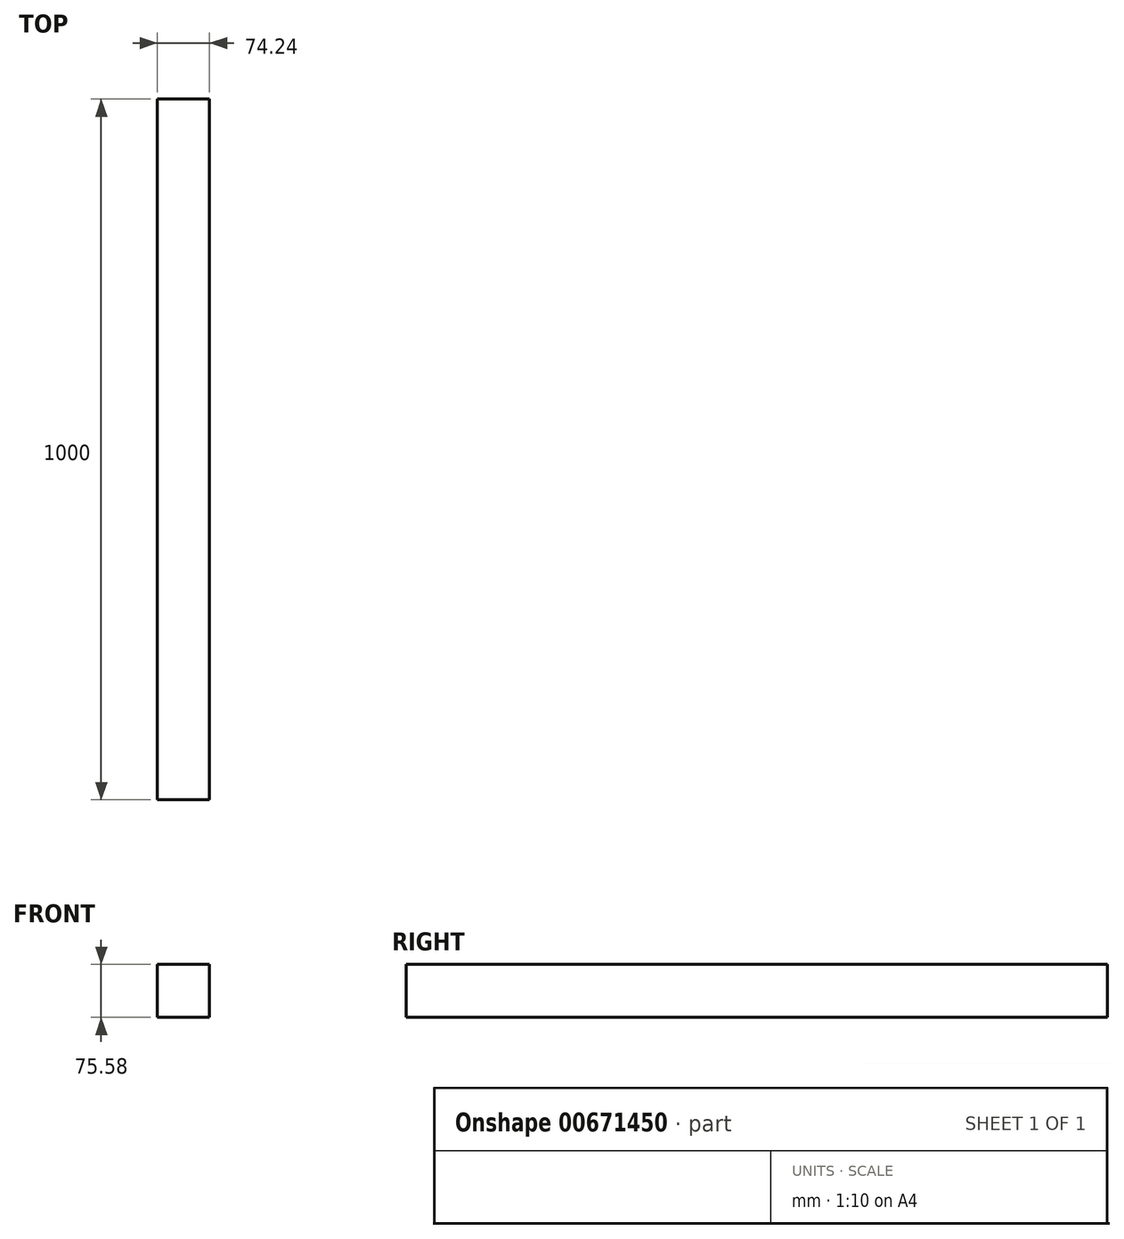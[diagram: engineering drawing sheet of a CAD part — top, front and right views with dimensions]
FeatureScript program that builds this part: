
annotation { "Feature Type Name" : "Feature", "Feature Type Description" : "" }
export const myFeature = defineFeature(function(context is Context, id is Id, definition is map)
    precondition{}
    {
        {
            var Q0;
            Q0=qCreatedBy(makeId("Front.planeOp"),FACE);
            var sketch = newSketch(context, id + "F0", { "sketchPlane" : qUnion([Q0])});
            skLineSegment(sketch, "E0.bottom", {"start": v(-74.24, 0) * mm, "end": v(0, 0) * mm});
            skLineSegment(sketch, "E0.top", {"start": v(-74.24, 75.58) * mm, "end": v(0, 75.58) * mm});
            skLineSegment(sketch, "E0.left", {"start": v(-74.24, 0) * mm, "end": v(-74.24, 75.58) * mm});
            skLineSegment(sketch, "E0.right", {"start": v(0, 0) * mm, "end": v(0, 75.58) * mm});
            skLineSegment(sketch, "E1.bottom", {"start": v(132.43, 50.6) * mm, "end": v(214.08, 50.6) * mm});
            skLineSegment(sketch, "E1.top", {"start": v(132.43, 13.66) * mm, "end": v(214.08, 13.66) * mm});
            skLineSegment(sketch, "E1.left", {"start": v(132.43, 50.6) * mm, "end": v(132.43, 13.66) * mm});
            skLineSegment(sketch, "E1.right", {"start": v(214.08, 50.6) * mm, "end": v(214.08, 13.66) * mm});
            skSolve(sketch);
        }
        {
            var Q0;
            Q0 = qSketchRegion(id + "F0", true);
            extrude(context, id + "F1", {"entities" : qUnion([Q0]), "depth" : 1000 * mm, "offsetDistance" : 25.4 * mm});
        }
        {
            var Q0;
            Q0=makeQuery(id+"F1.opExtrude","SWEPT_BODY",BODY,{"disambiguationData":[OSD([sQuery(id+"F0.wireOp",EDGE,"E1.bottom"),sQuery(id+"F0.wireOp",EDGE,"E1.top"),sQuery(id+"F0.wireOp",EDGE,"E1.left"),sQuery(id+"F0.wireOp",EDGE,"E1.right")])]});
            deleteBodies(context, id + "F2", {"entities" : qUnion([Q0])});
        }
    });
